# Revit family: Wand und Deckenkanal-WDK60060RW
name_source: partatom
category: Generic Models
revit_build: Autodesk Revit 2017 (Build: 20190508_0315(x64)
units: mm (PartAtom-declared; Revit-internal decimal feet)

## family parameters
Always vertical = Yes
Can host rebar = No
Cut with Voids When Loaded = No
Part Type = Normal
Room Calculation Point = No
Round Connector Dimension = Use Diameter
Shared = No
Work Plane-Based = No

## types (1)
- WDK60060RW
    Article Type = WDK60060RW
    GTIN = 4012196363018
    Height = 60 mm  [stored 0.19685 ft]
    Length = 2000 mm  [stored 6.56168 ft]
    Manufacturer = OBO BETTERMANN
    Manufacturer Art.No. = 6191193
    Material = Polyvinylchlorid
    URL = http://www.obo-bettermann.com
    Width = 60 mm  [stored 0.19685 ft]

note: [stored X ft] marks values corroborated as IEEE doubles in the binary element streams (Revit-internal decimal feet)

## geometry (parser evidence)
native form markers: Sweep x2
no freeform markers — native parametric forms only
